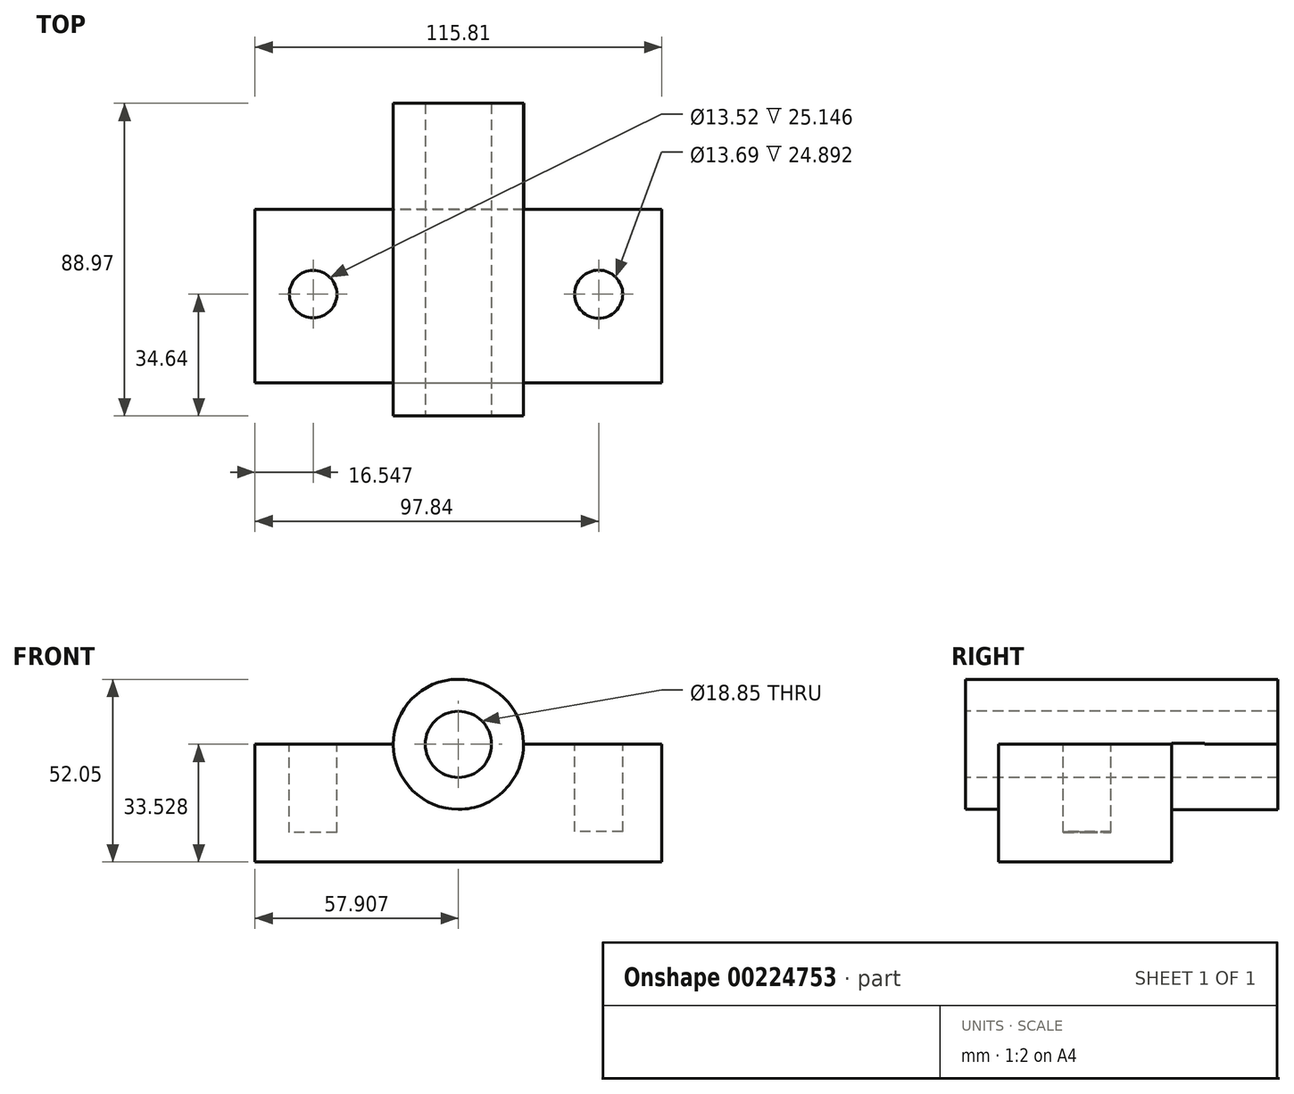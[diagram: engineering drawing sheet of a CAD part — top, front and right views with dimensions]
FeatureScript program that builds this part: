
annotation { "Feature Type Name" : "Feature", "Feature Type Description" : "" }
export const myFeature = defineFeature(function(context is Context, id is Id, definition is map)
    precondition{}
    {
        {
            var Q0;
            Q0=qCreatedBy(makeId("Top.planeOp"),FACE);
            var sketch = newSketch(context, id + "F0", { "sketchPlane" : qUnion([Q0])});
            skLineSegment(sketch, "E0.bottom", {"start": v(-55.9, 24.1) * mm, "end": v(59.9, 24.1) * mm});
            skLineSegment(sketch, "E0.top", {"start": v(-55.9, -25.24) * mm, "end": v(59.9, -25.24) * mm});
            skLineSegment(sketch, "E0.left", {"start": v(-55.9, 24.1) * mm, "end": v(-55.9, -25.24) * mm});
            skLineSegment(sketch, "E0.right", {"start": v(59.9, 24.1) * mm, "end": v(59.9, -25.24) * mm});
            skSolve(sketch);
        }
        {
            var Q0;
            Q0=makeQuery(id+"F0.imprint","IMPRINT",FACE,{"disambiguationData":[TD([[makeQuery(id+"F0.imprint","IMPRINT",EDGE,{"derivedFrom":sQuery(id+"F0.wireOp",EDGE,"E0.bottom")}),-1.0]])]});
            extrude(context, id + "F1", {"entities" : qUnion([Q0]), "depth" : 67.06 * mm});
        }
        {
            var Q0;
            Q0=makeQuery(id+"F1.opExtrude","SWEPT_FACE",FACE,{"disambiguationData":[OSD([sQuery(id+"F0.wireOp",EDGE,"E0.top")])]});
            var sketch = newSketch(context, id + "F2", { "sketchPlane" : qUnion([Q0])});
            skCircle(sketch, "E1", {"center": v(2, 33.53) * mm, "radius": 15.4 * mm});
            skLineSegment(sketch, "E2", {"start": v(2, 33.53) * mm, "end": v(59.9, 33.53) * mm});
            skLineSegment(sketch, "E3", {"start": v(-55.9, 33.53) * mm, "end": v(2, 33.53) * mm});
            skPoint(sketch, "E4.orphan", {"position": v(59.9, 67.06) * mm});
            skPoint(sketch, "E5.orphan", {"position": v(-55.9, 0) * mm});
            skCircle(sketch, "E6", {"center": v(2, 33.53) * mm, "radius": 9.43 * mm});
            skSolve(sketch);
        }
        {
            var Q0;
            {var subQ0=sQuery(id+"F2.wireOp",EDGE,"E3");var subQ1=sQuery(id+"F2.wireOp",EDGE,"E2");var subQ2=makeQuery(id+"F2.imprint","INTERSECT",VERTEX,{"derivedFrom":[subQ1,subQ0]});Q0=makeQuery(id+"F2.imprint","IMPRINT",FACE,{"disambiguationData":[TD([[makeQuery(id+"F2.imprint","IMPRINT",EDGE,{"disambiguationData":[TD([[subQ2,-1.0]])],"derivedFrom":subQ1}),1.0]])]});}
            var Q1;
            {var subQ0=sQuery(id+"F2.wireOp",EDGE,"E3");var subQ1=sQuery(id+"F2.wireOp",EDGE,"E2");var subQ2=makeQuery(id+"F2.imprint","INTERSECT",VERTEX,{"derivedFrom":[subQ1,subQ0]});Q1=makeQuery(id+"F2.imprint","IMPRINT",FACE,{"disambiguationData":[TD([[makeQuery(id+"F2.imprint","IMPRINT",EDGE,{"disambiguationData":[TD([[subQ2,-1.0]])],"derivedFrom":subQ1}),-1.0]])]});}
            extrude(context, id + "F3", {"entities" : qUnion([Q0, Q1]), "operationType" : NewBodyOperationType.REMOVE, "endBound" : BoundingType.THROUGH_ALL, "oppositeDirection" : true, "depth" : 25.4 * mm});
        }
        {
            var Q0;
            Q0=makeQuery(id+"F1.opExtrude","SWEPT_FACE",FACE,{"disambiguationData":[OSD([sQuery(id+"F0.wireOp",EDGE,"E0.bottom")])]});
            var sketch = newSketch(context, id + "F4", { "sketchPlane" : qUnion([Q0])});
            skCircle(sketch, "E7", {"center": v(-2, 33.53) * mm, "radius": 18.6 * mm});
            skPoint(sketch, "E8.trimOffspring.end.orphan", {"position": v(55.9, 67.06) * mm});
            skPoint(sketch, "E9.start.orphan", {"position": v(-59.9, 0) * mm});
            skPoint(sketch, "E10.orphan", {"position": v(55.9, 33.53) * mm});
            skPoint(sketch, "E11.orphan", {"position": v(-59.9, 33.53) * mm});
            skSolve(sketch);
        }
        {
            var Q0;
            {var subQ0=sQuery(id+"F4.wireOp",EDGE,"E7");var subQ1=sQuery(id+"F4.wireOp",EDGE,"jqVIVYJh-zH1L-gdFE-tPKG-OrK3S2NwULKQ");var subQ2=makeQuery(id+"F4.imprint","INTERSECT",VERTEX,{"derivedFrom":[subQ1,subQ0]});Q0=makeQuery(id+"F4.imprint","IMPRINT",FACE,{"disambiguationData":[TD([[makeQuery(id+"F4.imprint","IMPRINT",EDGE,{"disambiguationData":[TD([[subQ2,1.0]])],"derivedFrom":subQ0}),1.0]])]});}
            var Q1;
            {var subQ0=sQuery(id+"F4.wireOp",EDGE,"E7");var subQ1=sQuery(id+"F4.wireOp",EDGE,"jqVIVYJh-zH1L-gdFE-tPKG-OrK3S2NwULKQ");var subQ2=makeQuery(id+"F4.imprint","INTERSECT",VERTEX,{"derivedFrom":[subQ1,subQ0]});Q1=makeQuery(id+"F4.imprint","IMPRINT",FACE,{"disambiguationData":[TD([[makeQuery(id+"F4.imprint","IMPRINT",EDGE,{"disambiguationData":[TD([[subQ2,-1.0]])],"derivedFrom":subQ0}),1.0]])]});}
            extrude(context, id + "F5", {"entities" : qUnion([Q0, Q1]), "operationType" : NewBodyOperationType.ADD, "depth" : 30.23 * mm});
        }
        {
            var Q0;
            Q0=makeQuery(id+"F1.opExtrude","SWEPT_FACE",FACE,{"disambiguationData":[OSD([sQuery(id+"F0.wireOp",EDGE,"E0.top")])]});
            var sketch = newSketch(context, id + "F6", { "sketchPlane" : qUnion([Q0])});
            skCircle(sketch, "E12", {"center": v(2, 33.53) * mm, "radius": 18.52 * mm});
            skPoint(sketch, "E13.orphan", {"position": v(-55.9, 0) * mm});
            skPoint(sketch, "E14.orphan", {"position": v(59.9, 67.06) * mm});
            skSolve(sketch);
        }
        {
            var Q0;
            Q0=makeQuery(id+"F6.imprint","IMPRINT",FACE,{"disambiguationData":[TD([[makeQuery(id+"F6.imprint","IMPRINT",EDGE,{"derivedFrom":sQuery(id+"F6.wireOp",EDGE,"E12")}),1.0]])]});
            extrude(context, id + "F7", {"entities" : qUnion([Q0]), "operationType" : NewBodyOperationType.ADD, "depth" : 9.4 * mm});
        }
        {
            var Q0;
            Q0=makeQuery(id+"F1.opExtrude","SWEPT_FACE",FACE,{"disambiguationData":[OSD([sQuery(id+"F0.wireOp",EDGE,"E0.top")])]});
            var sketch = newSketch(context, id + "F8", { "sketchPlane" : qUnion([Q0])});
            skLineSegment(sketch, "E15", {"start": v(-55.9, 67.06) * mm, "end": v(-55.9, 33.53) * mm});
            skLineSegment(sketch, "E16", {"start": v(-55.9, 33.53) * mm, "end": v(59.9, 33.53) * mm});
            skLineSegment(sketch, "E17", {"start": v(59.9, 33.53) * mm, "end": v(59.9, 67.06) * mm});
            skLineSegment(sketch, "E18", {"start": v(59.9, 67.06) * mm, "end": v(-55.9, 67.06) * mm});
            skSolve(sketch);
        }
        {
            var Q0;
            {var subQ5=sQuery(id+"F8.wireOp",EDGE,"E15");Q0=makeQuery(id+"F8.imprint","IMPRINT",FACE,{"disambiguationData":[TD([[makeQuery(id+"F8.imprint","IMPRINT",EDGE,{"derivedFrom":subQ5}),1.0]])]});}
            extrude(context, id + "F9", {"entities" : qUnion([Q0]), "operationType" : NewBodyOperationType.REMOVE, "endBound" : BoundingType.THROUGH_ALL, "oppositeDirection" : true, "depth" : 25.4 * mm});
        }
        {
            var Q0;
            Q0=makeQuery(id+"F4.imprint","IMPRINT",FACE,{"disambiguationData":[TD([[makeQuery(id+"F4.imprint","IMPRINT",EDGE,{"derivedFrom":sQuery(id+"F4.wireOp",EDGE,"E7")}),1.0]])]});
            extrude(context, id + "F10", {"entities" : qUnion([Q0]), "operationType" : NewBodyOperationType.ADD, "depth" : 9.4 * mm});
        }
        {
            var Q0;
            Q0=makeQuery(id+"F10.opExtrude","CAP_FACE",FACE,{"disambiguationData":[OSD([sQuery(id+"F0.wireOp",EDGE,"E0.bottom"),sQuery(id+"F2.wireOp",EDGE,"E6"),sQuery(id+"F4.wireOp",EDGE,"E7")])],"isStart":false});
            var sketch = newSketch(context, id + "F11", { "sketchPlane" : qUnion([Q0])});
            skLineSegment(sketch, "E19", {"start": v(-20.6, 33.8) * mm, "end": v(16.6, 33.8) * mm});
            skSolve(sketch);
        }
        {
            var Q0;
            {var subQ0=sQuery(id+"F11.wireOp",EDGE,"E19");var subQ1=makeQuery(id+"F10.opExtrude","CAP_EDGE",EDGE,{"disambiguationData":[OSD([sQuery(id+"F4.wireOp",EDGE,"E7")])],"isStart":false});var subQ2=makeQuery(id+"F11.imprint","INTERSECT",VERTEX,{"disambiguationData":[OD(0.0)],"derivedFrom":[subQ1,subQ0]});Q0=makeQuery(id+"F11.imprint","IMPRINT",FACE,{"disambiguationData":[TD([[makeQuery(id+"F11.imprint","IMPRINT",EDGE,{"disambiguationData":[TD([[subQ2,1.0]])],"derivedFrom":subQ1}),1.0]])]});}
            extrude(context, id + "F12", {"entities" : qUnion([Q0]), "operationType" : NewBodyOperationType.REMOVE, "endBound" : BoundingType.THROUGH_ALL, "oppositeDirection" : true, "depth" : 25.4 * mm});
        }
        {
            var Q0;
            {var subQ0=sQuery(id+"F8.wireOp",EDGE,"E16");Q0=makeQuery(id+"F9.boolean.opBoolean","COPY",FACE,{"derivedFrom":makeQuery(id+"F9.opExtrude","SWEPT_FACE",FACE,{"disambiguationData":[OSD([subQ0]),TDD([makeQuery(id+"F8.imprint","IMPRINT",EDGE,{"disambiguationData":[TD([[makeQuery(id+"F8.imprint","INTERSECT",VERTEX,{"disambiguationData":[OD(0.0)],"derivedFrom":[makeQuery(id+"F7.opExtrude","CAP_EDGE",EDGE,{"disambiguationData":[OSD([sQuery(id+"F6.wireOp",EDGE,"E12")])],"isStart":true}),subQ0]}),1.0]])],"derivedFrom":subQ0})])]})});}
            var sketch = newSketch(context, id + "F13", { "sketchPlane" : qUnion([Q0])});
            skCircle(sketch, "E20", {"center": v(-39.36, 0) * mm, "radius": 6.76 * mm});
            skSolve(sketch);
        }
        {
            var Q0;
            {var subQ0=sQuery(id+"F8.wireOp",EDGE,"E16");Q0=makeQuery(id+"F9.boolean.opBoolean","COPY",FACE,{"derivedFrom":makeQuery(id+"F9.opExtrude","SWEPT_FACE",FACE,{"disambiguationData":[OSD([subQ0]),TDD([makeQuery(id+"F8.imprint","IMPRINT",EDGE,{"disambiguationData":[TD([[makeQuery(id+"F8.imprint","INTERSECT",VERTEX,{"disambiguationData":[OD(1.0)],"derivedFrom":[makeQuery(id+"F7.opExtrude","CAP_EDGE",EDGE,{"disambiguationData":[OSD([sQuery(id+"F6.wireOp",EDGE,"E12")])],"isStart":true}),subQ0]}),-1.0]])],"derivedFrom":subQ0})])]})});}
            var sketch = newSketch(context, id + "F14", { "sketchPlane" : qUnion([Q0])});
            skCircle(sketch, "E21", {"center": v(41.93, 0) * mm, "radius": 6.85 * mm});
            skSolve(sketch);
        }
        {
            var Q0;
            Q0=makeQuery(id+"F13.imprint","IMPRINT",FACE,{"disambiguationData":[TD([[makeQuery(id+"F13.imprint","IMPRINT",EDGE,{"derivedFrom":sQuery(id+"F13.wireOp",EDGE,"E20")}),1.0]])]});
            extrude(context, id + "F15", {"entities" : qUnion([Q0]), "operationType" : NewBodyOperationType.REMOVE, "oppositeDirection" : true, "depth" : 25.15 * mm});
        }
        {
            var Q0;
            Q0=makeQuery(id+"F14.imprint","IMPRINT",FACE,{"disambiguationData":[TD([[makeQuery(id+"F14.imprint","IMPRINT",EDGE,{"derivedFrom":sQuery(id+"F14.wireOp",EDGE,"E21")}),1.0]])]});
            extrude(context, id + "F16", {"entities" : qUnion([Q0]), "operationType" : NewBodyOperationType.REMOVE, "oppositeDirection" : true, "depth" : 24.9 * mm});
        }
    });
